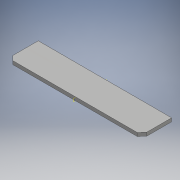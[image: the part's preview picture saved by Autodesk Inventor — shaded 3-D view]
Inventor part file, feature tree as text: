
AUTODESK INVENTOR PART (.ipt)
format: ipt  version: 2018 (Build 220112000, 112)  size: 123,904 bytes
history: native  units: mm
features: other x5, plane x1, sheet_metal_op x1, sketch x1, reference x1
ambient origin geometry x8: Origin, YZ Plane, XZ Plane, XY Plane, X Axis, Y Axis, Z Axis, Center Point
bodies: Solid1 (feature_tree)
feature tree (9):
  plane  "Work Plane1"
  sheet_metal_op  "Face1"
  other  "midtplan"
  sketch  "Sketch1"  dims[d3=45.0deg d4=7.171149mm d5=30.0mm d6=2.0mm d7=3.0mm]
  reference  "Reference1"
  other  "Plate1"
  parser-record x1  (decoder bookkeeping rows leaked as tree rows — omitted from the tree; the rows remain in map.json)
  other  "modul.iam"
  other  "plade:1"
note: 1 file-system path scrubbed to <path> (originals preserved in map.json)
